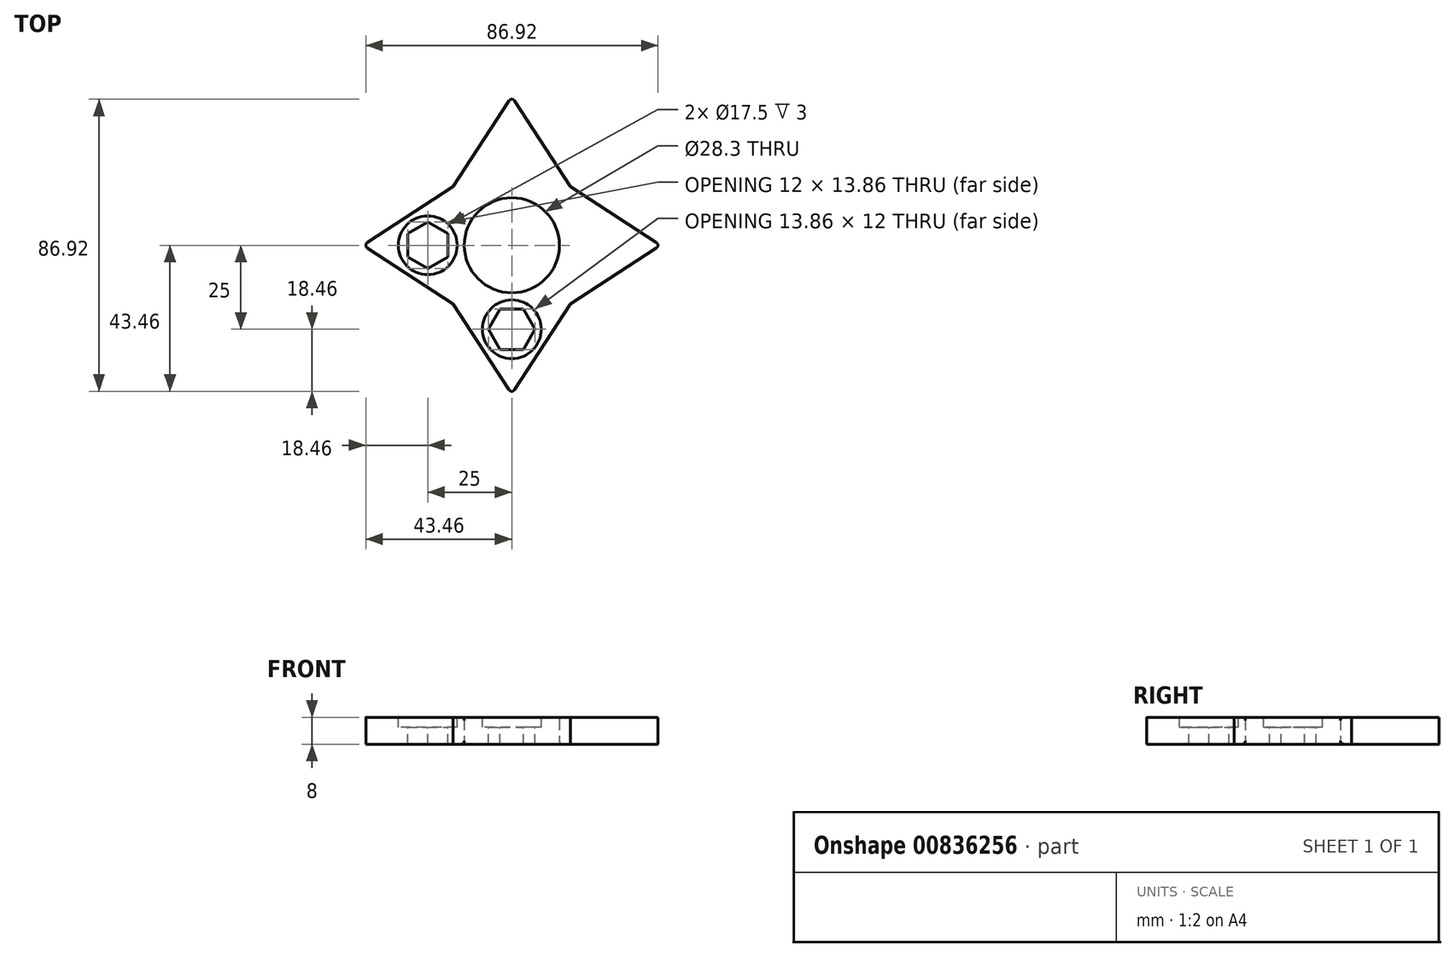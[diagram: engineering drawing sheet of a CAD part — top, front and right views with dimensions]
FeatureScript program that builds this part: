
annotation { "Feature Type Name" : "Feature", "Feature Type Description" : "" }
export const myFeature = defineFeature(function(context is Context, id is Id, definition is map)
    precondition{}
    {
        {
            var Q0;
            Q0=qCreatedBy(makeId("Top.planeOp"),FACE);
            var sketch = newSketch(context, id + "F0", { "sketchPlane" : qUnion([Q0])});
            skCircle(sketch, "E0", {"center": v(0, 0) * mm, "radius": 14.15 * mm});
            skLineSegment(sketch, "E1.bottom", {"start": v(17.5, -17.5) * mm, "end": v(-17.5, -17.5) * mm});
            skLineSegment(sketch, "E1.top", {"start": v(17.5, 17.5) * mm, "end": v(-17.5, 17.5) * mm});
            skLineSegment(sketch, "E1.left", {"start": v(17.5, -17.5) * mm, "end": v(17.5, 17.5) * mm});
            skLineSegment(sketch, "E1.right", {"start": v(-17.5, -17.5) * mm, "end": v(-17.5, 17.5) * mm});
            skLineSegment(sketch, "E2", {"start": v(-17.5, 17.5) * mm, "end": v(-44.3, 0) * mm});
            skLineSegment(sketch, "E3", {"start": v(-44.3, 0) * mm, "end": v(-17.5, -17.5) * mm});
            skLineSegment(sketch, "E4", {"start": v(-17.5, 17.5) * mm, "end": v(0, 44.3) * mm});
            skLineSegment(sketch, "E5", {"start": v(0, 44.3) * mm, "end": v(17.5, 17.5) * mm});
            skLineSegment(sketch, "E6", {"start": v(17.5, 17.5) * mm, "end": v(44.3, 0) * mm});
            skLineSegment(sketch, "E7", {"start": v(44.3, 0) * mm, "end": v(17.5, -17.5) * mm});
            skLineSegment(sketch, "E8", {"start": v(-17.5, -17.5) * mm, "end": v(0, -44.3) * mm});
            skLineSegment(sketch, "E9", {"start": v(0, -44.3) * mm, "end": v(17.5, -17.5) * mm});
            skSolve(sketch);
        }
        {
            var Q0;
            Q0=makeQuery(id+"F0.imprint","IMPRINT",FACE,{"disambiguationData":[TD([[makeQuery(id+"F0.imprint","IMPRINT",EDGE,{"derivedFrom":sQuery(id+"F0.wireOp",EDGE,"E1.bottom")}),1.0]])]});
            var Q1;
            Q1=makeQuery(id+"F0.imprint","IMPRINT",FACE,{"disambiguationData":[TD([[makeQuery(id+"F0.imprint","IMPRINT",EDGE,{"derivedFrom":sQuery(id+"F0.wireOp",EDGE,"E1.left")}),-1.0]])]});
            var Q2;
            Q2=makeQuery(id+"F0.imprint","IMPRINT",FACE,{"disambiguationData":[TD([[makeQuery(id+"F0.imprint","IMPRINT",EDGE,{"derivedFrom":sQuery(id+"F0.wireOp",EDGE,"E1.right")}),1.0]])]});
            var Q3;
            Q3=makeQuery(id+"F0.imprint","IMPRINT",FACE,{"disambiguationData":[TD([[makeQuery(id+"F0.imprint","IMPRINT",EDGE,{"derivedFrom":sQuery(id+"F0.wireOp",EDGE,"E0")}),-1.0]])]});
            var Q4;
            Q4=makeQuery(id+"F0.imprint","IMPRINT",FACE,{"disambiguationData":[TD([[makeQuery(id+"F0.imprint","IMPRINT",EDGE,{"derivedFrom":sQuery(id+"F0.wireOp",EDGE,"E1.top")}),-1.0]])]});
            extrude(context, id + "F1", {"entities" : qUnion([Q0, Q1, Q2, Q3, Q4]), "depth" : 8 * mm, "offsetDistance" : 25 * mm});
        }
        {
            var Q0;
            Q0=makeQuery(id+"F1.opExtrude","CAP_FACE",FACE,{"disambiguationData":[OSD([sQuery(id+"F0.wireOp",EDGE,"E0"),sQuery(id+"F0.wireOp",EDGE,"E2"),sQuery(id+"F0.wireOp",EDGE,"E3"),sQuery(id+"F0.wireOp",EDGE,"E4"),sQuery(id+"F0.wireOp",EDGE,"E5"),sQuery(id+"F0.wireOp",EDGE,"E6"),sQuery(id+"F0.wireOp",EDGE,"E7"),sQuery(id+"F0.wireOp",EDGE,"E8"),sQuery(id+"F0.wireOp",EDGE,"E9")])],"isStart":false});
            var sketch = newSketch(context, id + "F2", { "sketchPlane" : qUnion([Q0])});
            skCircle(sketch, "E10.cCircle", {"center": v(-25, 0) * mm, "radius": 6 * mm, "construction": true});
            skLineSegment(sketch, "E10.0", {"start": v(-19, 3.46) * mm, "end": v(-19, -3.46) * mm});
            skLineSegment(sketch, "E10.1", {"start": v(-19, -3.46) * mm, "end": v(-25, -6.93) * mm});
            skLineSegment(sketch, "E10.2", {"start": v(-25, -6.93) * mm, "end": v(-31, -3.46) * mm});
            skLineSegment(sketch, "E10.3", {"start": v(-31, -3.46) * mm, "end": v(-31, 3.46) * mm});
            skLineSegment(sketch, "E10.4", {"start": v(-31, 3.46) * mm, "end": v(-25, 6.93) * mm});
            skLineSegment(sketch, "E10.5", {"start": v(-25, 6.93) * mm, "end": v(-19, 3.46) * mm});
            skPoint(sketch, "E10.0.midPoint", {"position": v(-19, 0) * mm});
            skSolve(sketch);
        }
        {
            var Q0;
            Q0=makeQuery(id+"F2.imprint","IMPRINT",FACE,{"disambiguationData":[TD([[makeQuery(id+"F2.imprint","IMPRINT",EDGE,{"derivedFrom":sQuery(id+"F2.wireOp",EDGE,"E10.0")}),-1.0]])]});
            extrude(context, id + "F3", {"entities" : qUnion([Q0]), "operationType" : NewBodyOperationType.REMOVE, "oppositeDirection" : true, "depth" : 25 * mm, "offsetDistance" : 25 * mm});
        }
        {
            var Q0;
            Q0=makeQuery(id+"F1.opExtrude","CAP_FACE",FACE,{"disambiguationData":[OSD([sQuery(id+"F0.wireOp",EDGE,"E0"),sQuery(id+"F0.wireOp",EDGE,"E2"),sQuery(id+"F0.wireOp",EDGE,"E3"),sQuery(id+"F0.wireOp",EDGE,"E4"),sQuery(id+"F0.wireOp",EDGE,"E5"),sQuery(id+"F0.wireOp",EDGE,"E6"),sQuery(id+"F0.wireOp",EDGE,"E7"),sQuery(id+"F0.wireOp",EDGE,"E8"),sQuery(id+"F0.wireOp",EDGE,"E9")])],"isStart":false});
            var sketch = newSketch(context, id + "F4", { "sketchPlane" : qUnion([Q0])});
            skCircle(sketch, "E11", {"center": v(-25, 0) * mm, "radius": 8.75 * mm});
            skSolve(sketch);
        }
        {
            var Q0;
            Q0=makeQuery(id+"F4.imprint","IMPRINT",FACE,{"disambiguationData":[TD([[makeQuery(id+"F4.imprint","IMPRINT",EDGE,{"derivedFrom":sQuery(id+"F4.wireOp",EDGE,"E11")}),1.0]])]});
            extrude(context, id + "F5", {"entities" : qUnion([Q0]), "operationType" : NewBodyOperationType.REMOVE, "oppositeDirection" : true, "depth" : 3 * mm, "offsetDistance" : 25 * mm});
        }
        {
            var Q0;
            Q0=makeQuery(id+"F1.opExtrude","CAP_FACE",FACE,{"disambiguationData":[OSD([sQuery(id+"F0.wireOp",EDGE,"E0"),sQuery(id+"F0.wireOp",EDGE,"E2"),sQuery(id+"F0.wireOp",EDGE,"E3"),sQuery(id+"F0.wireOp",EDGE,"E4"),sQuery(id+"F0.wireOp",EDGE,"E5"),sQuery(id+"F0.wireOp",EDGE,"E6"),sQuery(id+"F0.wireOp",EDGE,"E7"),sQuery(id+"F0.wireOp",EDGE,"E8"),sQuery(id+"F0.wireOp",EDGE,"E9")])],"isStart":false});
            var sketch = newSketch(context, id + "F6", { "sketchPlane" : qUnion([Q0])});
            skCircle(sketch, "E12.cCircle", {"center": v(0, -25) * mm, "radius": 6 * mm, "construction": true});
            skLineSegment(sketch, "E12.0", {"start": v(-3.46, -19) * mm, "end": v(3.46, -19) * mm});
            skLineSegment(sketch, "E12.1", {"start": v(3.46, -19) * mm, "end": v(6.93, -25) * mm});
            skLineSegment(sketch, "E12.2", {"start": v(6.93, -25) * mm, "end": v(3.46, -31) * mm});
            skLineSegment(sketch, "E12.3", {"start": v(3.46, -31) * mm, "end": v(-3.46, -31) * mm});
            skLineSegment(sketch, "E12.4", {"start": v(-3.46, -31) * mm, "end": v(-6.93, -25) * mm});
            skLineSegment(sketch, "E12.5", {"start": v(-6.93, -25) * mm, "end": v(-3.46, -19) * mm});
            skPoint(sketch, "E12.0.midPoint", {"position": v(0, -19) * mm});
            skSolve(sketch);
        }
        {
            var Q0;
            Q0=makeQuery(id+"F6.imprint","IMPRINT",FACE,{"disambiguationData":[TD([[makeQuery(id+"F6.imprint","IMPRINT",EDGE,{"derivedFrom":sQuery(id+"F6.wireOp",EDGE,"E12.0")}),-1.0]])]});
            extrude(context, id + "F7", {"entities" : qUnion([Q0]), "operationType" : NewBodyOperationType.REMOVE, "oppositeDirection" : true, "depth" : 25 * mm, "offsetDistance" : 25 * mm});
        }
        {
            var Q0;
            Q0=makeQuery(id+"F1.opExtrude","CAP_FACE",FACE,{"disambiguationData":[OSD([sQuery(id+"F0.wireOp",EDGE,"E0"),sQuery(id+"F0.wireOp",EDGE,"E2"),sQuery(id+"F0.wireOp",EDGE,"E3"),sQuery(id+"F0.wireOp",EDGE,"E4"),sQuery(id+"F0.wireOp",EDGE,"E5"),sQuery(id+"F0.wireOp",EDGE,"E6"),sQuery(id+"F0.wireOp",EDGE,"E7"),sQuery(id+"F0.wireOp",EDGE,"E8"),sQuery(id+"F0.wireOp",EDGE,"E9")])],"isStart":false});
            var sketch = newSketch(context, id + "F8", { "sketchPlane" : qUnion([Q0])});
            skCircle(sketch, "E13", {"center": v(0, -25) * mm, "radius": 8.75 * mm});
            skSolve(sketch);
        }
        {
            var Q0;
            Q0=makeQuery(id+"F8.imprint","IMPRINT",FACE,{"disambiguationData":[TD([[makeQuery(id+"F8.imprint","IMPRINT",EDGE,{"derivedFrom":sQuery(id+"F8.wireOp",EDGE,"E13")}),1.0]])]});
            extrude(context, id + "F9", {"entities" : qUnion([Q0]), "operationType" : NewBodyOperationType.REMOVE, "oppositeDirection" : true, "depth" : 3 * mm, "offsetDistance" : 25 * mm});
        }
        {
            var Q0;
            Q0=makeQuery(id+"F1.opExtrude","SWEPT_EDGE",EDGE,{"disambiguationData":[OSD([sQuery(id+"F0.wireOp",EDGE,"E2"),sQuery(id+"F0.wireOp",EDGE,"E3")])]});
            var Q1;
            Q1=makeQuery(id+"F1.opExtrude","SWEPT_EDGE",EDGE,{"disambiguationData":[OSD([sQuery(id+"F0.wireOp",EDGE,"E4"),sQuery(id+"F0.wireOp",EDGE,"E5")])]});
            var Q2;
            Q2=makeQuery(id+"F1.opExtrude","SWEPT_EDGE",EDGE,{"disambiguationData":[OSD([sQuery(id+"F0.wireOp",EDGE,"E8"),sQuery(id+"F0.wireOp",EDGE,"E9")])]});
            var Q3;
            Q3=makeQuery(id+"F1.opExtrude","SWEPT_EDGE",EDGE,{"disambiguationData":[OSD([sQuery(id+"F0.wireOp",EDGE,"E6"),sQuery(id+"F0.wireOp",EDGE,"E7")])]});
            fillet(context, id + "F10", {"entities" : qUnion([Q0, Q1, Q2, Q3]), "radius" : 1 * mm, "tangentPropagation" : true, "allowEdgeOverflow" : false});
        }
        {
            var Q0;
            Q0=makeQuery(id+"F1.opExtrude","CAP_EDGE",EDGE,{"disambiguationData":[OSD([sQuery(id+"F0.wireOp",EDGE,"E0")])],"isStart":false});
            var Q1;
            Q1=makeQuery(id+"F1.opExtrude","CAP_EDGE",EDGE,{"disambiguationData":[OSD([sQuery(id+"F0.wireOp",EDGE,"E0")])],"isStart":true});
            fillet(context, id + "F11", {"entities" : qUnion([Q0, Q1]), "radius" : 0.9 * mm, "tangentPropagation" : true, "allowEdgeOverflow" : false});
        }
    });
